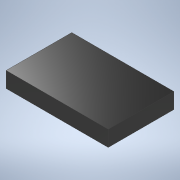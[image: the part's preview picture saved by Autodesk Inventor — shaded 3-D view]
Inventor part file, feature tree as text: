
AUTODESK INVENTOR PART (.ipt)
format: ipt  version: 2020 (Build 240168000, 168)  size: 93,184 bytes
history: native  units: in
note: dims shown in document units (in); Inventor stores cm internally (conversion verified against a paired STEP export)
features: extrude x1, sketch x1
ambient origin geometry x8: Origin, YZ Plane, XZ Plane, XY Plane, X Axis, Y Axis, Z Axis, Center Point
bodies: Solid1 (feature_tree)
feature tree (2):
  extrude  "Extrusion1"  Depth=0.63in
  sketch  "Sketch1"  dims[d0=0.98in d1=0.63in d2=0.15in d3=0.0in]
